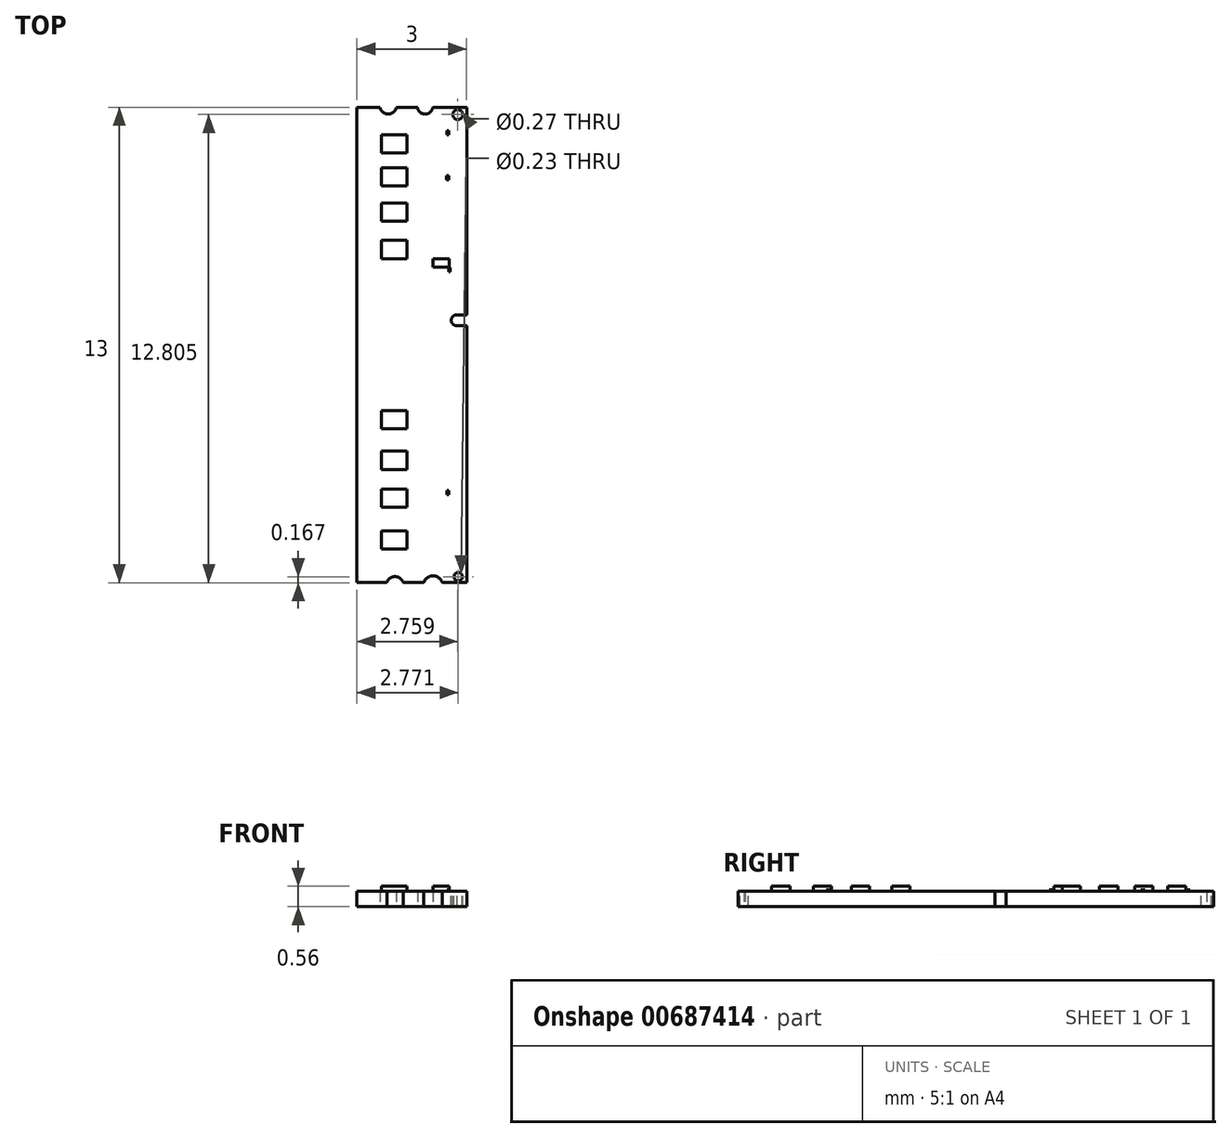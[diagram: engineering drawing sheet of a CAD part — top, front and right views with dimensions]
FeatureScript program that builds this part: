
annotation { "Feature Type Name" : "Feature", "Feature Type Description" : "" }
export const myFeature = defineFeature(function(context is Context, id is Id, definition is map)
    precondition{}
    {
        {
            var Q0;
            Q0=qCreatedBy(makeId("Top.planeOp"),FACE);
            var sketch = newSketch(context, id + "F0", { "sketchPlane" : qUnion([Q0])});
            skLineSegment(sketch, "E0.bottom", {"start": v(-17.32, 21.5) * mm, "end": v(-18.25, 21.5) * mm});
            skLineSegment(sketch, "E0.top", {"start": v(-17.32, 8.5) * mm, "end": v(-17.99, 8.5) * mm});
            skLineSegment(sketch, "E0.left", {"start": v(-17.32, 21.5) * mm, "end": v(-17.32, 8.5) * mm});
            skLineSegment(sketch, "E0.right", {"start": v(-20.32, 21.5) * mm, "end": v(-20.32, 8.5) * mm});
            skArc(sketch, "E1", {"start": v(-18.66, 21.5) * mm, "mid": v(-18.45, 21.32) * mm, "end": v(-18.25, 21.5) * mm});
            skArc(sketch, "E2", {"start": v(-19.05, 8.5) * mm, "mid": v(-19.28, 8.67) * mm, "end": v(-19.5, 8.5) * mm});
            skArc(sketch, "E3", {"start": v(-17.99, 8.5) * mm, "mid": v(-18.24, 8.7) * mm, "end": v(-18.49, 8.5) * mm});
            skLineSegment(sketch, "E4.trimOffspring", {"start": v(-19.5, 8.5) * mm, "end": v(-20.32, 8.5) * mm});
            skLineSegment(sketch, "E5.trimOffspring", {"start": v(-18.49, 8.5) * mm, "end": v(-19.05, 8.5) * mm});
            skLineSegment(sketch, "E6.trimOffspring", {"start": v(-19.69, 21.5) * mm, "end": v(-20.32, 21.5) * mm});
            skLineSegment(sketch, "E7.trimOffspring", {"start": v(-18.66, 21.5) * mm, "end": v(-19.24, 21.5) * mm});
            skArc(sketch, "E8", {"start": v(-19.69, 21.5) * mm, "mid": v(-19.46, 21.32) * mm, "end": v(-19.24, 21.5) * mm});
            skSolve(sketch);
        }
        {
            var Q0;
            Q0=makeQuery(id+"F0.imprint","IMPRINT",FACE,{"disambiguationData":[TD([[makeQuery(id+"F0.imprint","IMPRINT",EDGE,{"derivedFrom":sQuery(id+"F0.wireOp",EDGE,"E0.bottom")}),1.0]])]});
            extrude(context, id + "F1", {"entities" : qUnion([Q0]), "depth" : 0.43 * mm, "offsetDistance" : 25 * mm});
        }
        {
            var Q0;
            Q0=makeQuery(id+"F1.opExtrude","CAP_FACE",FACE,{"disambiguationData":[OSD([sQuery(id+"F0.wireOp",EDGE,"E0.bottom"),sQuery(id+"F0.wireOp",EDGE,"E0.top"),sQuery(id+"F0.wireOp",EDGE,"E0.left"),sQuery(id+"F0.wireOp",EDGE,"E0.right"),sQuery(id+"F0.wireOp",EDGE,"E1"),sQuery(id+"F0.wireOp",EDGE,"E2"),sQuery(id+"F0.wireOp",EDGE,"E3"),sQuery(id+"F0.wireOp",EDGE,"E4.trimOffspring"),sQuery(id+"F0.wireOp",EDGE,"E5.trimOffspring"),sQuery(id+"F0.wireOp",EDGE,"E6.trimOffspring"),sQuery(id+"F0.wireOp",EDGE,"E7.trimOffspring"),sQuery(id+"F0.wireOp",EDGE,"E8")])],"isStart":false});
            var sketch = newSketch(context, id + "F2", { "sketchPlane" : qUnion([Q0])});
            skCircle(sketch, "E9", {"center": v(-17.55, 8.67) * mm, "radius": 0.11 * mm});
            skCircle(sketch, "E10", {"center": v(-17.56, 21.3) * mm, "radius": 0.14 * mm});
            skSolve(sketch);
        }
        {
            var Q0;
            Q0=makeQuery(id+"F2.imprint","IMPRINT",FACE,{"disambiguationData":[TD([[makeQuery(id+"F2.imprint","IMPRINT",EDGE,{"derivedFrom":sQuery(id+"F2.wireOp",EDGE,"E9")}),1.0]])]});
            var Q1;
            Q1=makeQuery(id+"F2.imprint","IMPRINT",FACE,{"disambiguationData":[TD([[makeQuery(id+"F2.imprint","IMPRINT",EDGE,{"derivedFrom":sQuery(id+"F2.wireOp",EDGE,"E10")}),1.0]])]});
            extrude(context, id + "F3", {"entities" : qUnion([Q0, Q1]), "operationType" : NewBodyOperationType.REMOVE, "oppositeDirection" : true, "depth" : 25 * mm, "offsetDistance" : 25 * mm});
        }
        {
            var Q0;
            Q0=makeQuery(id+"F1.opExtrude","CAP_FACE",FACE,{"disambiguationData":[OSD([sQuery(id+"F0.wireOp",EDGE,"E0.bottom"),sQuery(id+"F0.wireOp",EDGE,"E0.top"),sQuery(id+"F0.wireOp",EDGE,"E0.left"),sQuery(id+"F0.wireOp",EDGE,"E0.right"),sQuery(id+"F0.wireOp",EDGE,"E1"),sQuery(id+"F0.wireOp",EDGE,"E2"),sQuery(id+"F0.wireOp",EDGE,"E3"),sQuery(id+"F0.wireOp",EDGE,"E4.trimOffspring"),sQuery(id+"F0.wireOp",EDGE,"E5.trimOffspring"),sQuery(id+"F0.wireOp",EDGE,"E6.trimOffspring"),sQuery(id+"F0.wireOp",EDGE,"E7.trimOffspring"),sQuery(id+"F0.wireOp",EDGE,"E8")])],"isStart":false});
            var sketch = newSketch(context, id + "F4", { "sketchPlane" : qUnion([Q0])});
            skPoint(sketch, "E11.firstSnap0", {"position": v(-18.95, 21.5) * mm});
            skLineSegment(sketch, "E11.bottom", {"start": v(-18.95, 20.75) * mm, "end": v(-19.65, 20.75) * mm});
            skLineSegment(sketch, "E11.top", {"start": v(-18.95, 20.25) * mm, "end": v(-19.65, 20.25) * mm});
            skLineSegment(sketch, "E11.left", {"start": v(-18.95, 20.75) * mm, "end": v(-18.95, 20.25) * mm});
            skLineSegment(sketch, "E11.right", {"start": v(-19.65, 20.75) * mm, "end": v(-19.65, 20.25) * mm});
            skLineSegment(sketch, "E12.bottom", {"start": v(-18.95, 19.85) * mm, "end": v(-19.65, 19.85) * mm});
            skLineSegment(sketch, "E12.top", {"start": v(-18.95, 19.35) * mm, "end": v(-19.65, 19.35) * mm});
            skLineSegment(sketch, "E12.left", {"start": v(-18.95, 19.85) * mm, "end": v(-18.95, 19.35) * mm});
            skLineSegment(sketch, "E12.right", {"start": v(-19.65, 19.85) * mm, "end": v(-19.65, 19.35) * mm});
            skLineSegment(sketch, "E13.bottom", {"start": v(-18.95, 18.89) * mm, "end": v(-19.65, 18.89) * mm});
            skLineSegment(sketch, "E13.top", {"start": v(-18.95, 18.39) * mm, "end": v(-19.65, 18.39) * mm});
            skLineSegment(sketch, "E13.left", {"start": v(-18.95, 18.89) * mm, "end": v(-18.95, 18.39) * mm});
            skLineSegment(sketch, "E13.right", {"start": v(-19.65, 18.89) * mm, "end": v(-19.65, 18.39) * mm});
            skLineSegment(sketch, "E14.bottom", {"start": v(-18.95, 17.86) * mm, "end": v(-19.65, 17.86) * mm});
            skLineSegment(sketch, "E14.top", {"start": v(-18.95, 17.36) * mm, "end": v(-19.65, 17.36) * mm});
            skLineSegment(sketch, "E14.left", {"start": v(-18.95, 17.86) * mm, "end": v(-18.95, 17.36) * mm});
            skLineSegment(sketch, "E14.right", {"start": v(-19.65, 17.86) * mm, "end": v(-19.65, 17.36) * mm});
            skLineSegment(sketch, "E15.bottom", {"start": v(-18.95, 9.42) * mm, "end": v(-19.65, 9.42) * mm});
            skLineSegment(sketch, "E15.top", {"start": v(-18.95, 9.92) * mm, "end": v(-19.65, 9.92) * mm});
            skLineSegment(sketch, "E15.left", {"start": v(-18.95, 9.42) * mm, "end": v(-18.95, 9.92) * mm});
            skLineSegment(sketch, "E15.right", {"start": v(-19.65, 9.42) * mm, "end": v(-19.65, 9.92) * mm});
            skLineSegment(sketch, "E16.bottom", {"start": v(-18.95, 10.56) * mm, "end": v(-19.65, 10.56) * mm});
            skLineSegment(sketch, "E16.top", {"start": v(-18.95, 11.06) * mm, "end": v(-19.65, 11.06) * mm});
            skLineSegment(sketch, "E16.left", {"start": v(-18.95, 10.56) * mm, "end": v(-18.95, 11.06) * mm});
            skLineSegment(sketch, "E16.right", {"start": v(-19.65, 10.56) * mm, "end": v(-19.65, 11.06) * mm});
            skLineSegment(sketch, "E17.bottom", {"start": v(-18.95, 11.6) * mm, "end": v(-19.65, 11.6) * mm});
            skLineSegment(sketch, "E17.top", {"start": v(-18.95, 12.1) * mm, "end": v(-19.65, 12.1) * mm});
            skLineSegment(sketch, "E17.left", {"start": v(-18.95, 11.6) * mm, "end": v(-18.95, 12.1) * mm});
            skLineSegment(sketch, "E17.right", {"start": v(-19.65, 11.6) * mm, "end": v(-19.65, 12.1) * mm});
            skLineSegment(sketch, "E18.bottom", {"start": v(-18.95, 12.7) * mm, "end": v(-19.65, 12.7) * mm});
            skLineSegment(sketch, "E18.top", {"start": v(-18.95, 13.2) * mm, "end": v(-19.65, 13.2) * mm});
            skLineSegment(sketch, "E18.left", {"start": v(-18.95, 12.7) * mm, "end": v(-18.95, 13.2) * mm});
            skLineSegment(sketch, "E18.right", {"start": v(-19.65, 12.7) * mm, "end": v(-19.65, 13.2) * mm});
            skLineSegment(sketch, "E19.bottom", {"start": v(-18.25, 17.36) * mm, "end": v(-17.8, 17.36) * mm});
            skLineSegment(sketch, "E19.top", {"start": v(-18.25, 17.14) * mm, "end": v(-17.8, 17.14) * mm});
            skLineSegment(sketch, "E19.left", {"start": v(-18.25, 17.36) * mm, "end": v(-18.25, 17.14) * mm});
            skLineSegment(sketch, "E19.right", {"start": v(-17.8, 17.36) * mm, "end": v(-17.8, 17.14) * mm});
            skSolve(sketch);
        }
        {
            var Q0;
            Q0=makeQuery(id+"F4.imprint","IMPRINT",FACE,{"disambiguationData":[TD([[makeQuery(id+"F4.imprint","IMPRINT",EDGE,{"derivedFrom":sQuery(id+"F4.wireOp",EDGE,"E11.bottom")}),1.0]])]});
            var Q1;
            Q1=makeQuery(id+"F4.imprint","IMPRINT",FACE,{"disambiguationData":[TD([[makeQuery(id+"F4.imprint","IMPRINT",EDGE,{"derivedFrom":sQuery(id+"F4.wireOp",EDGE,"E12.bottom")}),1.0]])]});
            var Q2;
            Q2=makeQuery(id+"F4.imprint","IMPRINT",FACE,{"disambiguationData":[TD([[makeQuery(id+"F4.imprint","IMPRINT",EDGE,{"derivedFrom":sQuery(id+"F4.wireOp",EDGE,"E13.bottom")}),1.0]])]});
            var Q3;
            Q3=makeQuery(id+"F4.imprint","IMPRINT",FACE,{"disambiguationData":[TD([[makeQuery(id+"F4.imprint","IMPRINT",EDGE,{"derivedFrom":sQuery(id+"F4.wireOp",EDGE,"E14.bottom")}),1.0]])]});
            var Q4;
            Q4=makeQuery(id+"F4.imprint","IMPRINT",FACE,{"disambiguationData":[TD([[makeQuery(id+"F4.imprint","IMPRINT",EDGE,{"derivedFrom":sQuery(id+"F4.wireOp",EDGE,"E19.bottom")}),-1.0]])]});
            var Q5;
            Q5=makeQuery(id+"F4.imprint","IMPRINT",FACE,{"disambiguationData":[TD([[makeQuery(id+"F4.imprint","IMPRINT",EDGE,{"derivedFrom":sQuery(id+"F4.wireOp",EDGE,"E18.bottom")}),-1.0]])]});
            var Q6;
            Q6=makeQuery(id+"F4.imprint","IMPRINT",FACE,{"disambiguationData":[TD([[makeQuery(id+"F4.imprint","IMPRINT",EDGE,{"derivedFrom":sQuery(id+"F4.wireOp",EDGE,"E17.bottom")}),-1.0]])]});
            var Q7;
            Q7=makeQuery(id+"F4.imprint","IMPRINT",FACE,{"disambiguationData":[TD([[makeQuery(id+"F4.imprint","IMPRINT",EDGE,{"derivedFrom":sQuery(id+"F4.wireOp",EDGE,"E16.bottom")}),-1.0]])]});
            var Q8;
            Q8=makeQuery(id+"F4.imprint","IMPRINT",FACE,{"disambiguationData":[TD([[makeQuery(id+"F4.imprint","IMPRINT",EDGE,{"derivedFrom":sQuery(id+"F4.wireOp",EDGE,"E15.bottom")}),-1.0]])]});
            extrude(context, id + "F5", {"entities" : qUnion([Q0, Q1, Q2, Q3, Q4, Q5, Q6, Q7, Q8]), "operationType" : NewBodyOperationType.ADD, "depth" : 0.13 * mm, "offsetDistance" : 25 * mm});
        }
        {
            var Q0;
            Q0=makeQuery(id+"F1.opExtrude","CAP_FACE",FACE,{"disambiguationData":[OSD([sQuery(id+"F0.wireOp",EDGE,"E0.bottom"),sQuery(id+"F0.wireOp",EDGE,"E0.top"),sQuery(id+"F0.wireOp",EDGE,"E0.left"),sQuery(id+"F0.wireOp",EDGE,"E0.right"),sQuery(id+"F0.wireOp",EDGE,"E1"),sQuery(id+"F0.wireOp",EDGE,"E2"),sQuery(id+"F0.wireOp",EDGE,"E3"),sQuery(id+"F0.wireOp",EDGE,"E4.trimOffspring"),sQuery(id+"F0.wireOp",EDGE,"E5.trimOffspring"),sQuery(id+"F0.wireOp",EDGE,"E6.trimOffspring"),sQuery(id+"F0.wireOp",EDGE,"E7.trimOffspring"),sQuery(id+"F0.wireOp",EDGE,"E8")])],"isStart":false});
            var sketch = newSketch(context, id + "F6", { "sketchPlane" : qUnion([Q0])});
            skArc(sketch, "E20", {"start": v(-17.58, 15.83) * mm, "mid": v(-17.74, 15.68) * mm, "end": v(-17.58, 15.53) * mm});
            skLineSegment(sketch, "E21", {"start": v(-17.58, 15.83) * mm, "end": v(-17.32, 15.83) * mm});
            skLineSegment(sketch, "E22", {"start": v(-17.58, 15.53) * mm, "end": v(-17.32, 15.53) * mm});
            skSolve(sketch);
        }
        {
            var Q0;
            Q0=makeQuery(id+"F6.imprint","IMPRINT",FACE,{"disambiguationData":[TD([[makeQuery(id+"F6.imprint","IMPRINT",EDGE,{"derivedFrom":sQuery(id+"F6.wireOp",EDGE,"E20")}),1.0]])]});
            extrude(context, id + "F7", {"entities" : qUnion([Q0]), "operationType" : NewBodyOperationType.REMOVE, "oppositeDirection" : true, "depth" : 25 * mm, "offsetDistance" : 25 * mm});
        }
        {
            var Q0;
            Q0=makeQuery(id+"F1.opExtrude","CAP_FACE",FACE,{"disambiguationData":[OSD([sQuery(id+"F0.wireOp",EDGE,"E0.bottom"),sQuery(id+"F0.wireOp",EDGE,"E0.top"),sQuery(id+"F0.wireOp",EDGE,"E0.left"),sQuery(id+"F0.wireOp",EDGE,"E0.right"),sQuery(id+"F0.wireOp",EDGE,"E1"),sQuery(id+"F0.wireOp",EDGE,"E2"),sQuery(id+"F0.wireOp",EDGE,"E3"),sQuery(id+"F0.wireOp",EDGE,"E4.trimOffspring"),sQuery(id+"F0.wireOp",EDGE,"E5.trimOffspring"),sQuery(id+"F0.wireOp",EDGE,"E6.trimOffspring"),sQuery(id+"F0.wireOp",EDGE,"E7.trimOffspring"),sQuery(id+"F0.wireOp",EDGE,"E8")])],"isStart":false});
            var sketch = newSketch(context, id + "F8", { "sketchPlane" : qUnion([Q0])});
            skLineSegment(sketch, "E23.bottom", {"start": v(-17.85, 20.75) * mm, "end": v(-17.8, 20.75) * mm});
            skLineSegment(sketch, "E23.top", {"start": v(-17.85, 20.86) * mm, "end": v(-17.8, 20.86) * mm});
            skLineSegment(sketch, "E23.left", {"start": v(-17.85, 20.75) * mm, "end": v(-17.85, 20.86) * mm});
            skLineSegment(sketch, "E23.right", {"start": v(-17.8, 20.75) * mm, "end": v(-17.8, 20.86) * mm});
            skLineSegment(sketch, "E24.bottom", {"start": v(-17.8, 19.63) * mm, "end": v(-17.87, 19.63) * mm});
            skLineSegment(sketch, "E24.top", {"start": v(-17.8, 19.52) * mm, "end": v(-17.87, 19.52) * mm});
            skLineSegment(sketch, "E24.left", {"start": v(-17.8, 19.63) * mm, "end": v(-17.8, 19.52) * mm});
            skLineSegment(sketch, "E24.right", {"start": v(-17.87, 19.63) * mm, "end": v(-17.87, 19.52) * mm});
            skLineSegment(sketch, "E25.bottom", {"start": v(-17.8, 17.12) * mm, "end": v(-17.77, 17.12) * mm});
            skLineSegment(sketch, "E25.top", {"start": v(-17.8, 17.01) * mm, "end": v(-17.77, 17.01) * mm});
            skLineSegment(sketch, "E25.left", {"start": v(-17.8, 17.12) * mm, "end": v(-17.8, 17.01) * mm});
            skLineSegment(sketch, "E25.right", {"start": v(-17.77, 17.12) * mm, "end": v(-17.77, 17.01) * mm});
            skLineSegment(sketch, "E26.bottom", {"start": v(-17.8, 11.02) * mm, "end": v(-17.86, 11.02) * mm});
            skLineSegment(sketch, "E26.top", {"start": v(-17.8, 10.91) * mm, "end": v(-17.86, 10.91) * mm});
            skLineSegment(sketch, "E26.left", {"start": v(-17.8, 11.02) * mm, "end": v(-17.8, 10.91) * mm});
            skLineSegment(sketch, "E26.right", {"start": v(-17.86, 11.02) * mm, "end": v(-17.86, 10.91) * mm});
            skSolve(sketch);
        }
        {
            var Q0;
            Q0=makeQuery(id+"F8.imprint","IMPRINT",FACE,{"disambiguationData":[TD([[makeQuery(id+"F8.imprint","IMPRINT",EDGE,{"derivedFrom":sQuery(id+"F8.wireOp",EDGE,"E23.bottom")}),1.0]])]});
            var Q1;
            Q1=makeQuery(id+"F8.imprint","IMPRINT",FACE,{"disambiguationData":[TD([[makeQuery(id+"F8.imprint","IMPRINT",EDGE,{"derivedFrom":sQuery(id+"F8.wireOp",EDGE,"E24.bottom")}),1.0]])]});
            var Q2;
            Q2=makeQuery(id+"F8.imprint","IMPRINT",FACE,{"disambiguationData":[TD([[makeQuery(id+"F8.imprint","IMPRINT",EDGE,{"derivedFrom":sQuery(id+"F8.wireOp",EDGE,"E25.bottom")}),-1.0]])]});
            var Q3;
            Q3=makeQuery(id+"F8.imprint","IMPRINT",FACE,{"disambiguationData":[TD([[makeQuery(id+"F8.imprint","IMPRINT",EDGE,{"derivedFrom":sQuery(id+"F8.wireOp",EDGE,"E26.bottom")}),1.0]])]});
            extrude(context, id + "F9", {"entities" : qUnion([Q0, Q1, Q2, Q3]), "operationType" : NewBodyOperationType.ADD, "depth" : 0.03 * mm, "offsetDistance" : 25 * mm});
        }
    });
